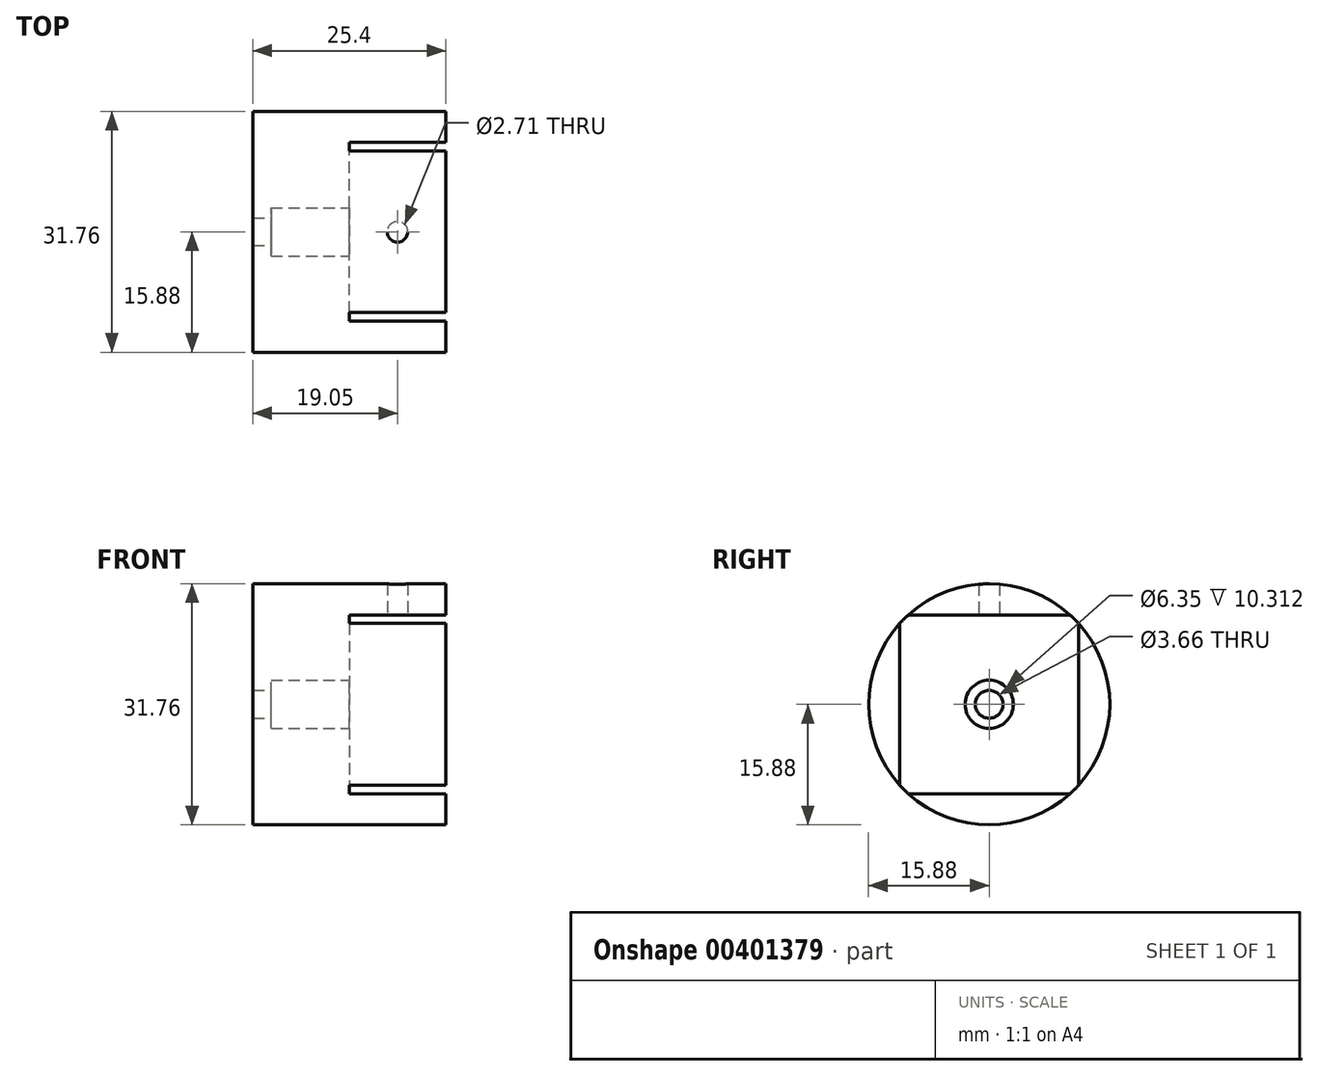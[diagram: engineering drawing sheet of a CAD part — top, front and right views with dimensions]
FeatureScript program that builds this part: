
annotation { "Feature Type Name" : "Feature", "Feature Type Description" : "" }
export const myFeature = defineFeature(function(context is Context, id is Id, definition is map)
    precondition{}
    {
        {
            var Q0;
            Q0=qCreatedBy(makeId("Right.planeOp"),FACE);
            var sketch = newSketch(context, id + "F0", { "sketchPlane" : qUnion([Q0])});
            skCircle(sketch, "E0", {"center": v(0, 0) * mm, "radius": 15.88 * mm});
            skSolve(sketch);
        }
        {
            var Q0;
            Q0=qSketchRegion(id+"F0",true);
            extrude(context, id + "F1", {"entities" : qUnion([Q0]), "depth" : 25.4 * mm});
        }
        {
            var Q0;
            Q0=makeQuery(id+"F1.opExtrude","CAP_FACE",FACE,{"disambiguationData":[OSD([sQuery(id+"F0.wireOp",EDGE,"E0")])],"isStart":false});
            var sketch = newSketch(context, id + "F2", { "sketchPlane" : qUnion([Q0])});
            skLineSegment(sketch, "E1.bottom", {"start": v(-11.77, 11.77) * mm, "end": v(11.77, 11.77) * mm});
            skLineSegment(sketch, "E1.top", {"start": v(-11.77, -11.77) * mm, "end": v(11.77, -11.77) * mm});
            skLineSegment(sketch, "E1.left", {"start": v(-11.77, 11.77) * mm, "end": v(-11.77, -11.77) * mm});
            skLineSegment(sketch, "E1.right", {"start": v(11.77, 11.77) * mm, "end": v(11.77, -11.77) * mm});
            skPoint(sketch, "E1.middle", {"position": v(0, 0) * mm});
            skSolve(sketch);
        }
        {
            var Q0;
            Q0=qSketchRegion(id+"F2",true);
            extrude(context, id + "F3", {"entities" : qUnion([Q0]), "operationType" : NewBodyOperationType.REMOVE, "oppositeDirection" : true, "depth" : 12.7 * mm});
        }
        {
            var Q0;
            Q0=makeQuery(id+"F1.opExtrude","CAP_FACE",FACE,{"disambiguationData":[OSD([sQuery(id+"F0.wireOp",EDGE,"E0")])],"isStart":false});
            var sketch = newSketch(context, id + "F4", { "sketchPlane" : qUnion([Q0])});
            skCircle(sketch, "E2", {"center": v(0, 0) * mm, "radius": 3.18 * mm});
            skSolve(sketch);
        }
        {
            var Q0;
            Q0=qSketchRegion(id+"F4",true);
            extrude(context, id + "F5", {"entities" : qUnion([Q0]), "operationType" : NewBodyOperationType.REMOVE, "oppositeDirection" : true, "depth" : 23.01 * mm});
        }
        {
            var Q0;
            Q0=makeQuery(id+"F3.boolean.opBoolean","COPY",FACE,{"derivedFrom":makeQuery(id+"F3.opExtrude","CAP_FACE",FACE,{"disambiguationData":[OSD([sQuery(id+"F2.wireOp",EDGE,"E1.bottom"),sQuery(id+"F2.wireOp",EDGE,"E1.top"),sQuery(id+"F2.wireOp",EDGE,"E1.left"),sQuery(id+"F2.wireOp",EDGE,"E1.right")])],"isStart":false})});
            var sketch = newSketch(context, id + "F6", { "sketchPlane" : qUnion([Q0])});
            skCircle(sketch, "E3", {"center": v(0, 0) * mm, "radius": 1.83 * mm});
            skSolve(sketch);
        }
        {
            var Q0;
            Q0=qSketchRegion(id+"F6",true);
            extrude(context, id + "F7", {"entities" : qUnion([Q0]), "operationType" : NewBodyOperationType.REMOVE, "endBound" : BoundingType.THROUGH_ALL, "oppositeDirection" : true, "depth" : 25.4 * mm});
        }
        {
            var Q0;
            Q0=makeQuery(id+"F3.boolean.opBoolean","COPY",FACE,{"derivedFrom":makeQuery(id+"F3.opExtrude","SWEPT_FACE",FACE,{"disambiguationData":[OSD([sQuery(id+"F2.wireOp",EDGE,"E1.bottom")])]})});
            var sketch = newSketch(context, id + "F8", { "sketchPlane" : qUnion([Q0])});
            skCircle(sketch, "E4", {"center": v(19.05, 0) * mm, "radius": 1.35 * mm});
            skLineSegment(sketch, "E5", {"start": v(12.7, 0) * mm, "end": v(19.05, 0) * mm, "construction": true});
            skLineSegment(sketch, "E6", {"start": v(19.05, 0) * mm, "end": v(25.4, 0) * mm, "construction": true});
            skSolve(sketch);
        }
        {
            var Q0;
            Q0 = qSketchRegion(id + "F8", true);
            extrude(context, id + "F9", {"entities" : qUnion([Q0]), "operationType" : NewBodyOperationType.REMOVE, "endBound" : BoundingType.THROUGH_ALL, "oppositeDirection" : true, "depth" : 25.4 * mm});
        }
    });
